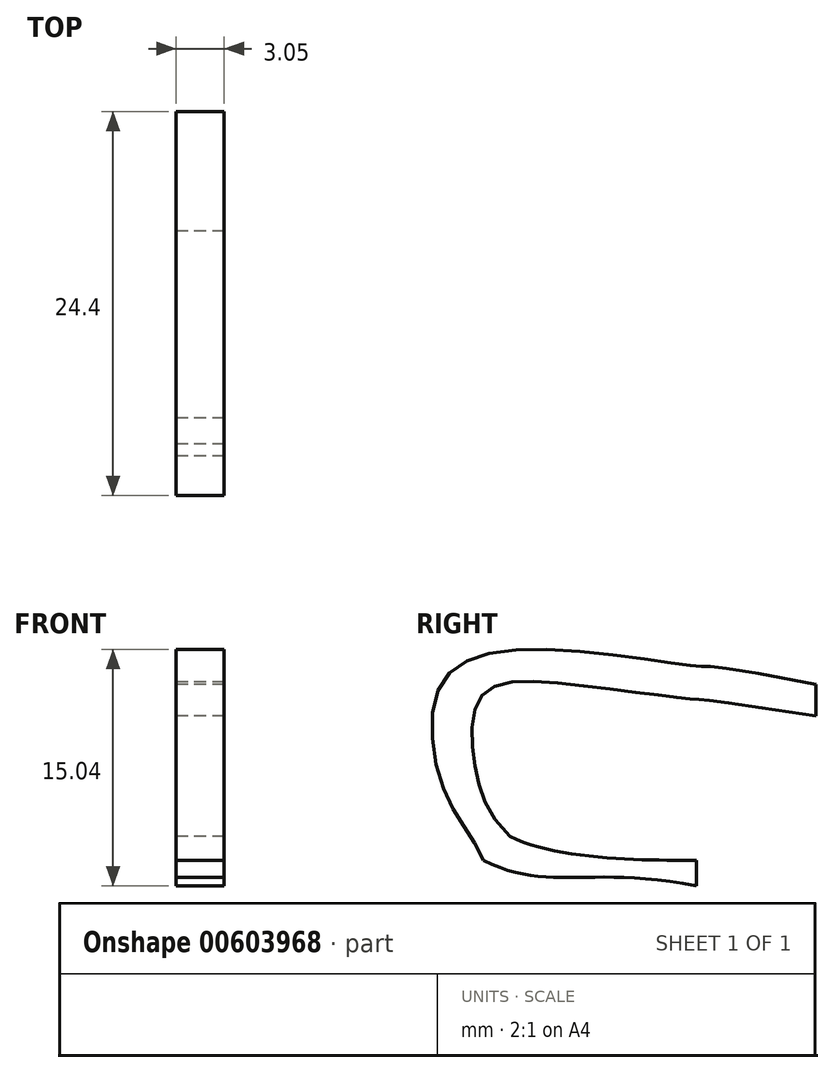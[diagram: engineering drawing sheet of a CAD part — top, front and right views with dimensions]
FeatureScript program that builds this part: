
annotation { "Feature Type Name" : "Feature", "Feature Type Description" : "" }
export const myFeature = defineFeature(function(context is Context, id is Id, definition is map)
    precondition{}
    {
        {
            var Q0;
            Q0=qCreatedBy(makeId("Right.planeOp"),FACE);
            var sketch = newSketch(context, id + "F0", { "sketchPlane" : qUnion([Q0])});
            skFitSpline(sketch, "E0", {"points": [v(0, 0) * mm, v(-2.46, 4.34) * mm, v(-2.66, 11.23) * mm, v(3.54, 13.4) * mm, v(13.27, 12.36) * mm, v(21.12, 11.16) * mm], "startDerivative": vector(-10.78, 27.1) * mm, "endDerivative": vector(107.2, -21.23) * mm});
            skFitSpline(sketch, "E1", {"points": [v(21.12, 9.17) * mm, v(12.83, 10.28) * mm, v(5.75, 11.16) * mm, v(0, 10.59) * mm, v(-0.6, 6.36) * mm, v(1.67, 1.5) * mm], "startDerivative": vector(-97.11, 15.05) * mm, "endDerivative": vector(25.46, -25.53) * mm});
            skFitSpline(sketch, "E2", {"points": [v(1.67, 1.5) * mm, v(13.54, 0) * mm], "startDerivative": vector(9.38, -4.53) * mm, "endDerivative": vector(9.76, 0) * mm});
            skFitSpline(sketch, "E3", {"points": [v(0, 0) * mm, v(13.54, -1.63) * mm], "startDerivative": vector(12.3, -6.19) * mm, "endDerivative": vector(20.76, -4.06) * mm});
            skLineSegment(sketch, "E4", {"start": v(21.12, 9.17) * mm, "end": v(21.12, 11.16) * mm});
            skLineSegment(sketch, "E5", {"start": v(13.54, 0) * mm, "end": v(13.54, -1.63) * mm});
            skSolve(sketch);
        }
        {
            var Q0;
            Q0=makeQuery(id+"F0.imprint","IMPRINT",FACE,{"disambiguationData":[TD([[makeQuery(id+"F0.imprint","IMPRINT",EDGE,{"derivedFrom":sQuery(id+"F0.wireOp",EDGE,"E0")}),-1.0]])]});
            extrude(context, id + "F1", {"entities" : qUnion([Q0]), "depth" : 3.05 * mm, "offsetDistance" : 25.4 * mm});
        }
    });
